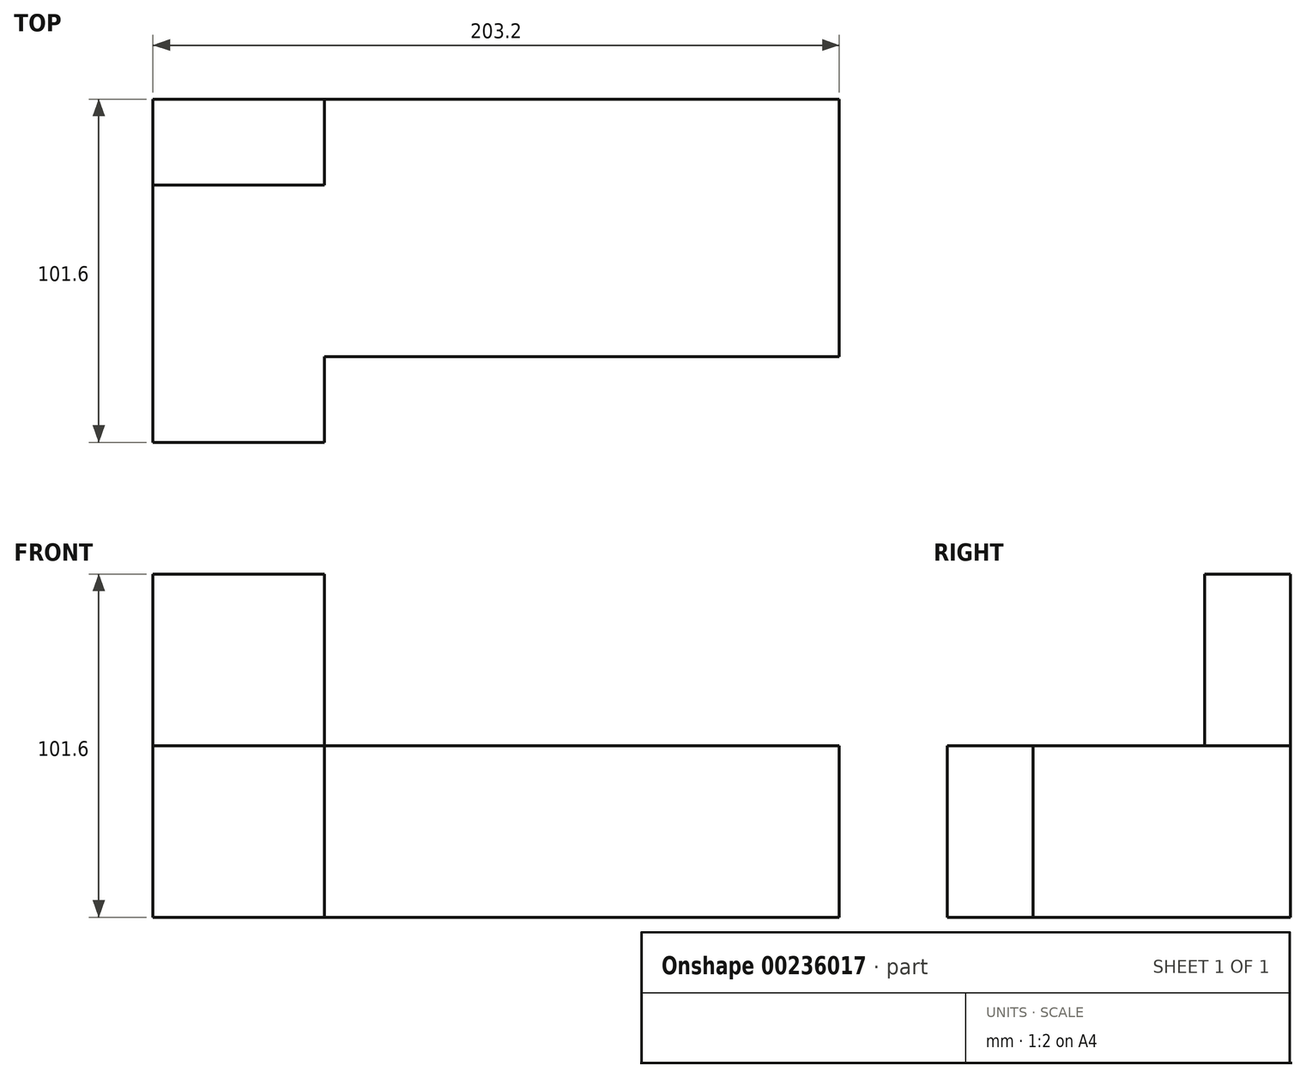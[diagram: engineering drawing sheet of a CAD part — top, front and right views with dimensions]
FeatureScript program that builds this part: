
annotation { "Feature Type Name" : "Feature", "Feature Type Description" : "" }
export const myFeature = defineFeature(function(context is Context, id is Id, definition is map)
    precondition{}
    {
        {
            var Q0;
            Q0=qCreatedBy(makeId("Top.planeOp"),FACE);
            var sketch = newSketch(context, id + "F0", { "sketchPlane" : qUnion([Q0])});
            skLineSegment(sketch, "E0.bottom", {"start": v(-131.78, -17.41) * mm, "end": v(-80.98, -17.41) * mm});
            skLineSegment(sketch, "E0.top", {"start": v(-131.78, 84.19) * mm, "end": v(-80.98, 84.19) * mm});
            skLineSegment(sketch, "E0.left", {"start": v(-131.78, -17.41) * mm, "end": v(-131.78, 84.19) * mm});
            skLineSegment(sketch, "E0.right", {"start": v(-80.98, -17.41) * mm, "end": v(-80.98, 84.19) * mm});
            skSolve(sketch);
        }
        {
            var Q0;
            Q0=makeQuery(id+"F0.imprint","IMPRINT",FACE,{"disambiguationData":[TD([[makeQuery(id+"F0.imprint","IMPRINT",EDGE,{"derivedFrom":sQuery(id+"F0.wireOp",EDGE,"E0.bottom")}),1.0]])]});
            extrude(context, id + "F1", {"entities" : qUnion([Q0]), "depth" : 50.8 * mm});
        }
        {
            var Q0;
            Q0=makeQuery(id+"F1.opExtrude","CAP_FACE",FACE,{"disambiguationData":[OSD([sQuery(id+"F0.wireOp",EDGE,"E0.bottom"),sQuery(id+"F0.wireOp",EDGE,"E0.top"),sQuery(id+"F0.wireOp",EDGE,"E0.left"),sQuery(id+"F0.wireOp",EDGE,"E0.right")])],"isStart":false});
            var sketch = newSketch(context, id + "F2", { "sketchPlane" : qUnion([Q0])});
            skLineSegment(sketch, "E1.bottom", {"start": v(-131.78, 84.19) * mm, "end": v(-80.98, 84.19) * mm});
            skLineSegment(sketch, "E1.top", {"start": v(-131.78, 58.79) * mm, "end": v(-80.98, 58.79) * mm});
            skLineSegment(sketch, "E1.left", {"start": v(-131.78, 84.19) * mm, "end": v(-131.78, 58.79) * mm});
            skLineSegment(sketch, "E1.right", {"start": v(-80.98, 84.19) * mm, "end": v(-80.98, 58.79) * mm});
            skSolve(sketch);
        }
        {
            var Q0;
            Q0=makeQuery(id+"F2.imprint","IMPRINT",FACE,{"disambiguationData":[TD([[makeQuery(id+"F2.imprint","IMPRINT",EDGE,{"derivedFrom":sQuery(id+"F2.wireOp",EDGE,"E1.bottom")}),-1.0]])]});
            extrude(context, id + "F3", {"entities" : qUnion([Q0]), "operationType" : NewBodyOperationType.ADD, "depth" : 50.8 * mm});
        }
        {
            var Q0;
            Q0=makeQuery(id+"F3.boolean.opBoolean","MERGE",FACE,{"derivedFrom":[makeQuery(id+"F1.opExtrude","SWEPT_FACE",FACE,{"disambiguationData":[OSD([sQuery(id+"F0.wireOp",EDGE,"E0.right")])]}),makeQuery(id+"F3.opExtrude","SWEPT_FACE",FACE,{"disambiguationData":[OSD([sQuery(id+"F2.wireOp",EDGE,"E1.right")])]})]});
            var sketch = newSketch(context, id + "F4", { "sketchPlane" : qUnion([Q0])});
            skLineSegment(sketch, "E2.bottom", {"start": v(-17.41, 50.8) * mm, "end": v(7.99, 50.8) * mm});
            skLineSegment(sketch, "E2.top", {"start": v(-17.41, 0) * mm, "end": v(7.99, 0) * mm});
            skLineSegment(sketch, "E2.left", {"start": v(-17.41, 50.8) * mm, "end": v(-17.41, 0) * mm});
            skLineSegment(sketch, "E2.right", {"start": v(7.99, 50.8) * mm, "end": v(7.99, 0) * mm});
            skSolve(sketch);
        }
        {
            var Q0;
            {var subQ1=sQuery(id+"F4.wireOp",EDGE,"E2.right");Q0=makeQuery(id+"F4.imprint","IMPRINT",FACE,{"disambiguationData":[TD([[makeQuery(id+"F4.imprint","IMPRINT",EDGE,{"derivedFrom":subQ1}),1.0]])]});}
            extrude(context, id + "F5", {"entities" : qUnion([Q0]), "operationType" : NewBodyOperationType.ADD, "depth" : 152.4 * mm});
        }
        {
            var Q0;
            {var subQ0=sQuery(id+"F2.wireOp",EDGE,"E1.top");Q0=makeQuery(id+"F5.boolean.opBoolean","MERGE",FACE,{"derivedFrom":[makeQuery(id+"F3.opExtrude","SWEPT_FACE",FACE,{"disambiguationData":[OSD([subQ0])]}),makeQuery(id+"F5.opExtrude","SWEPT_FACE",FACE,{"disambiguationData":[OSD([sQuery(id+"F0.wireOp",EDGE,"E0.right"),subQ0,sQuery(id+"F2.wireOp",EDGE,"E1.right")])]})]});}
            var sketch = newSketch(context, id + "F6", { "sketchPlane" : qUnion([Q0])});
            skLineSegment(sketch, "E3.bottom", {"start": v(-80.98, 101.6) * mm, "end": v(71.42, 101.6) * mm});
            skLineSegment(sketch, "E3.top", {"start": v(-80.98, 50.8) * mm, "end": v(71.42, 50.8) * mm});
            skLineSegment(sketch, "E3.left", {"start": v(-80.98, 101.6) * mm, "end": v(-80.98, 50.8) * mm});
            skLineSegment(sketch, "E3.right", {"start": v(71.42, 101.6) * mm, "end": v(71.42, 50.8) * mm});
            skSolve(sketch);
        }
        {
            var Q0;
            Q0=makeQuery(id+"F6.imprint","IMPRINT",FACE,{"disambiguationData":[TD([[makeQuery(id+"F6.imprint","IMPRINT",EDGE,{"derivedFrom":sQuery(id+"F6.wireOp",EDGE,"E3.bottom")}),-1.0]])]});
            extrude(context, id + "F7", {"entities" : qUnion([Q0]), "operationType" : NewBodyOperationType.REMOVE, "oppositeDirection" : true, "depth" : 25.4 * mm});
        }
    });
